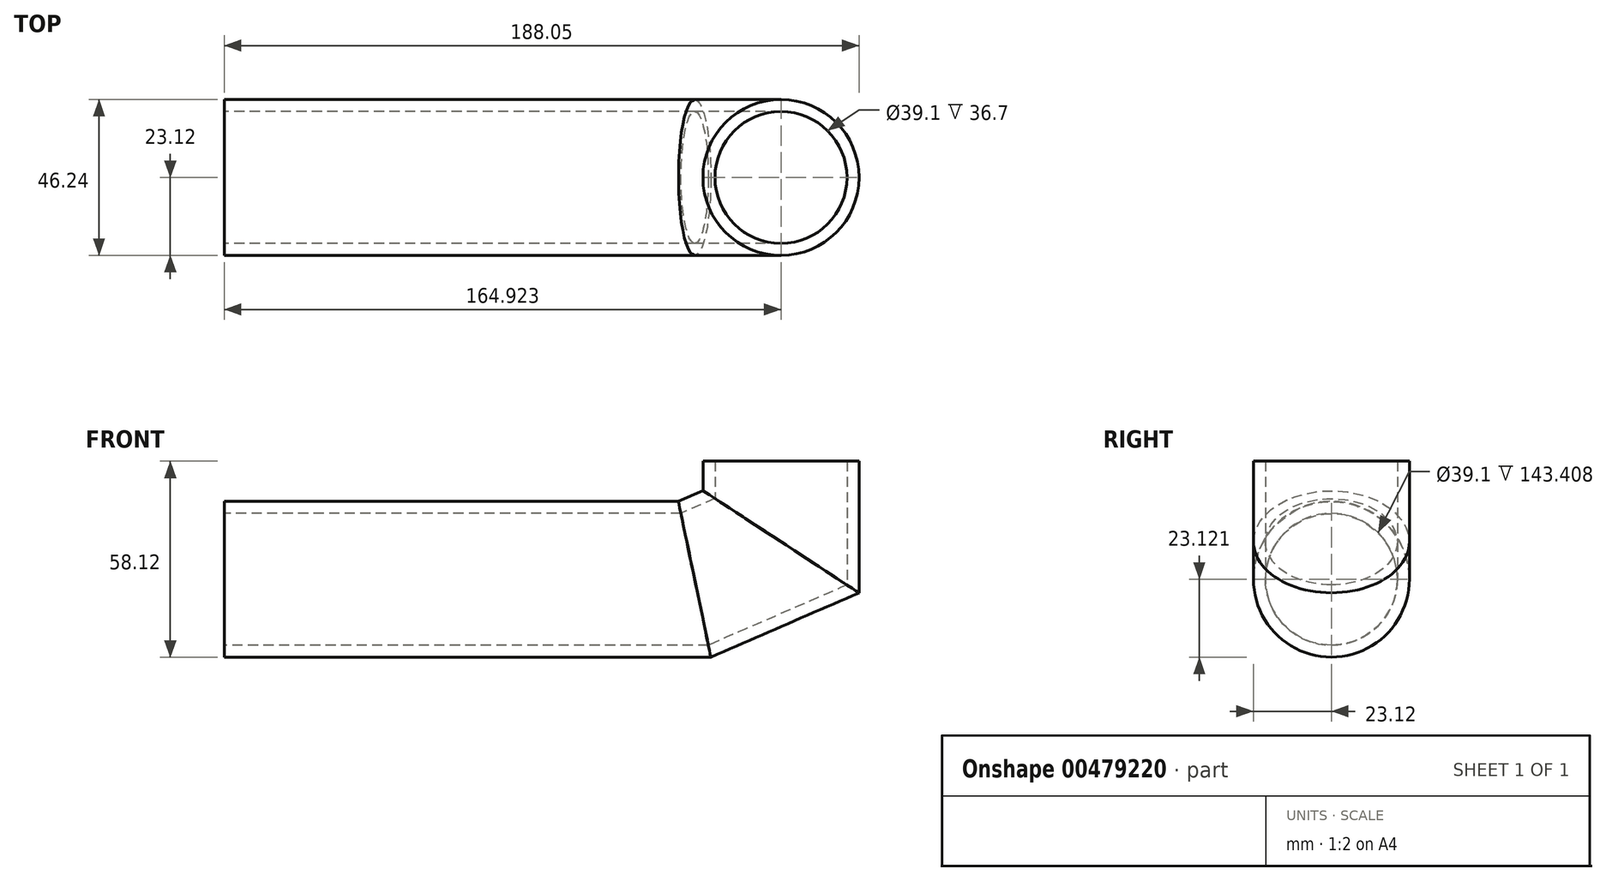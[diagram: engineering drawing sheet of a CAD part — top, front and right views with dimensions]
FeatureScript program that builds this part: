
annotation { "Feature Type Name" : "Feature", "Feature Type Description" : "" }
export const myFeature = defineFeature(function(context is Context, id is Id, definition is map)
    precondition{}
    {
        {
            var Q0;
            Q0=qCreatedBy(makeId("Front.planeOp"),FACE);
            var sketch = newSketch(context, id + "F0", { "sketchPlane" : qUnion([Q0])});
            skLineSegment(sketch, "E0", {"start": v(42.6, -38.77) * mm, "end": v(3.66, -42.88) * mm});
            skLineSegment(sketch, "E1", {"start": v(3.8, -45.45) * mm, "end": v(46.25, -40.97) * mm});
            skLineSegment(sketch, "E2", {"start": v(3.66, -42.85) * mm, "end": v(-100.2, -42.85) * mm});
            skLineSegment(sketch, "E3", {"start": v(-100.2, -45.45) * mm, "end": v(0, -45.45) * mm});
            skLineSegment(sketch, "E4", {"start": v(-90.61, -45.66) * mm, "end": v(-90.61, -45.45) * mm});
            skLineSegment(sketch, "E5", {"start": v(-100.2, -42.88) * mm, "end": v(-100.2, -45.45) * mm});
            skLineSegment(sketch, "E6", {"start": v(-47.47, -45.45) * mm, "end": v(-52.82, -45.45) * mm});
            skLineSegment(sketch, "E7", {"start": v(0, -45.45) * mm, "end": v(3.8, -45.45) * mm});
            skLineSegment(sketch, "E8", {"start": v(0, -14.62) * mm, "end": v(-100.2, -14.62) * mm});
            skLineSegment(sketch, "E9", {"start": v(-100.2, -17.15) * mm, "end": v(3.66, -17.15) * mm});
            skLineSegment(sketch, "E10", {"start": v(-90.61, -14.62) * mm, "end": v(-90.61, -14.41) * mm});
            skLineSegment(sketch, "E11", {"start": v(-100.2, -14.62) * mm, "end": v(-100.2, -17.19) * mm});
            skLineSegment(sketch, "E12", {"start": v(-52.82, -14.62) * mm, "end": v(-47.47, -14.62) * mm});
            skLineSegment(sketch, "E13", {"start": v(0, 0) * mm, "end": v(0, -14.62) * mm});
            skLineSegment(sketch, "E14", {"start": v(3.58, 0) * mm, "end": v(0, 0) * mm});
            skLineSegment(sketch, "E15", {"start": v(3.66, -14.14) * mm, "end": v(3.58, 0) * mm});
            skLineSegment(sketch, "E16", {"start": v(3.66, -17.19) * mm, "end": v(3.66, -14.14) * mm});
            skLineSegment(sketch, "E17", {"start": v(42.6, -14.14) * mm, "end": v(42.6, -38.77) * mm});
            skLineSegment(sketch, "E18", {"start": v(46.25, -40.97) * mm, "end": v(46.25, 0) * mm});
            skLineSegment(sketch, "E19", {"start": v(42.68, 0) * mm, "end": v(42.6, -14.14) * mm});
            skLineSegment(sketch, "E20", {"start": v(46.25, 0) * mm, "end": v(42.68, 0) * mm});
            skLineSegment(sketch, "E21", {"start": v(23.12, 0) * mm, "end": v(23.12, -18.88) * mm});
            skLineSegment(sketch, "E22", {"start": v(-99.8, -30) * mm, "end": v(-2.46, -30) * mm});
            skLineSegment(sketch, "E23", {"start": v(-2.46, -30) * mm, "end": v(23.12, -18.88) * mm});
            skSolve(sketch);
        }
        {
            var Q0;
            Q0=qCreatedBy(makeId("Top.planeOp"),FACE);
            var sketch = newSketch(context, id + "F1", { "sketchPlane" : qUnion([Q0])});
            skCircle(sketch, "E24", {"center": v(23.12, 0) * mm, "radius": 19.55 * mm});
            skCircle(sketch, "E25", {"center": v(23.12, 0) * mm, "radius": 23.12 * mm});
            skSolve(sketch);
        }
        {
            var Q0;
            Q0=makeQuery(id+"F1.imprint","IMPRINT",FACE,{"disambiguationData":[TD([[makeQuery(id+"F1.imprint","IMPRINT",EDGE,{"derivedFrom":sQuery(id+"F1.wireOp",EDGE,"E24")}),-1.0]])]});
            var Q1;
            Q1=sQuery(id+"F0.wireOp",EDGE,"E21");
            var Q2;
            Q2=sQuery(id+"F0.wireOp",EDGE,"E23");
            var Q3;
            Q3=sQuery(id+"F0.wireOp",EDGE,"E22");
            sweep(context, id + "F2", {"profiles" : qUnion([Q0]), "path" : qUnion([Q1, Q2, Q3])});
        }
        {
            var Q0;
            Q0=makeQuery(id+"F1.imprint","IMPRINT",FACE,{"disambiguationData":[TD([[makeQuery(id+"F1.imprint","IMPRINT",EDGE,{"derivedFrom":sQuery(id+"F1.wireOp",EDGE,"E24")}),-1.0]])]});
            extrude(context, id + "F3", {"entities" : qUnion([Q0]), "operationType" : NewBodyOperationType.ADD, "depth" : 5 * mm, "offsetDistance" : 25 * mm});
        }
        {
            var Q0;
            Q0=makeQuery(id+"F2.opSweep","CAP_FACE",FACE,{"disambiguationData":[OSD([sQuery(id+"F0.wireOp",VERTEX,"E22.start"),sQuery(id+"F1.wireOp",EDGE,"E24"),sQuery(id+"F1.wireOp",EDGE,"E25")])],"isStart":false});
            extrude(context, id + "F4", {"entities" : qUnion([Q0]), "operationType" : NewBodyOperationType.ADD, "depth" : 42 * mm, "offsetDistance" : 25 * mm});
        }
    });
